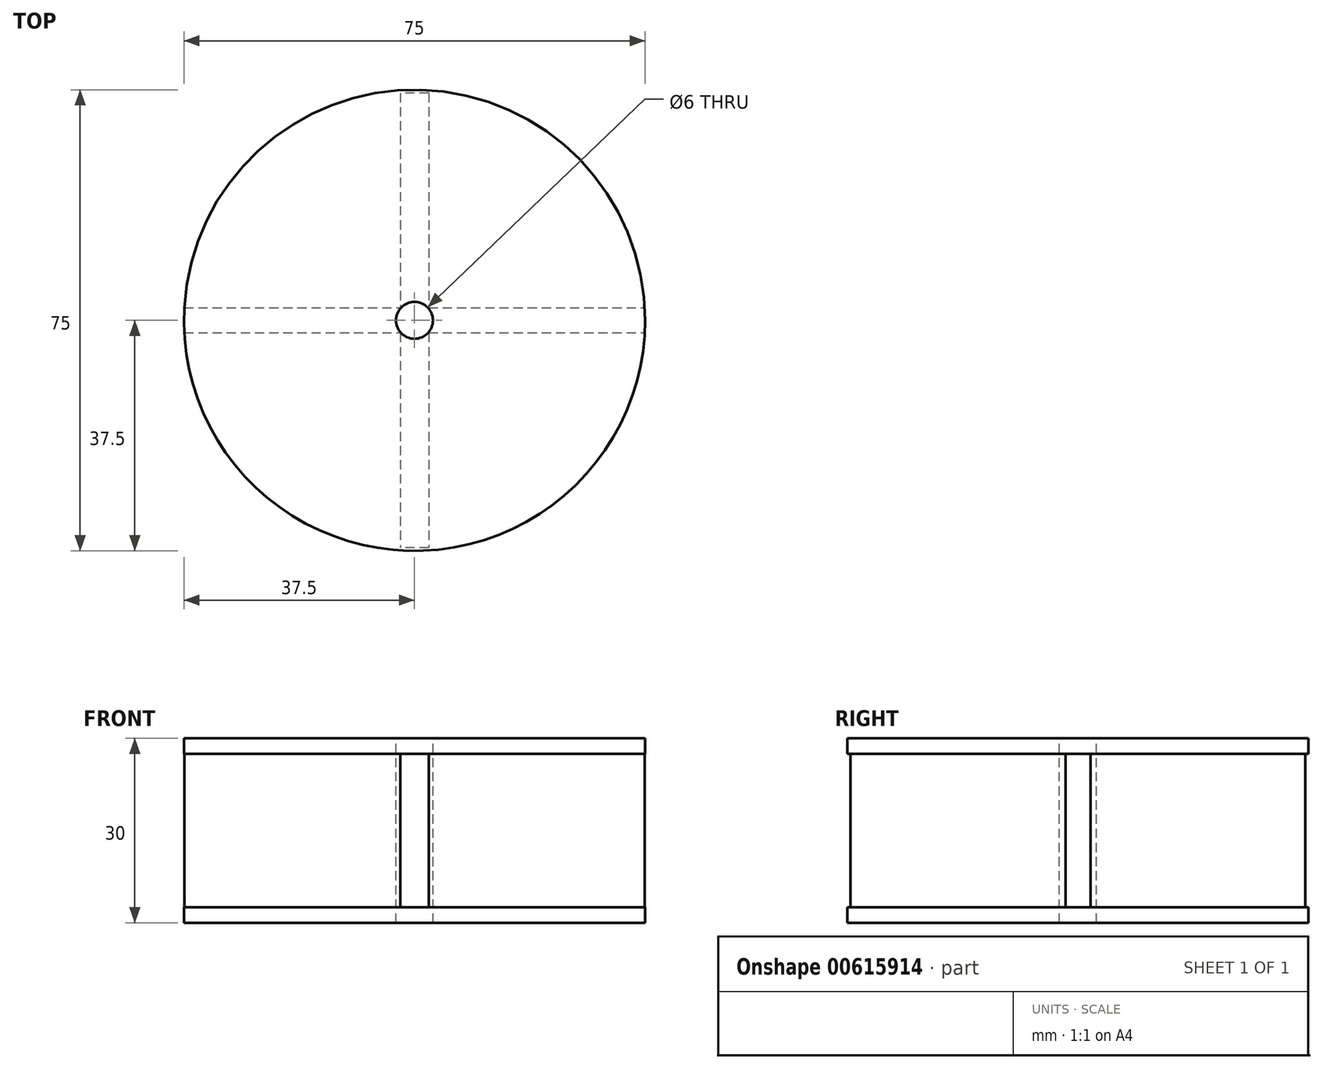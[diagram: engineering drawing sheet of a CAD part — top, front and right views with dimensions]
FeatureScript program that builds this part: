
annotation { "Feature Type Name" : "Feature", "Feature Type Description" : "" }
export const myFeature = defineFeature(function(context is Context, id is Id, definition is map)
    precondition{}
    {
        {
            var Q0;
            Q0=qCreatedBy(makeId("Top.planeOp"),FACE);
            var sketch = newSketch(context, id + "F0", { "sketchPlane" : qUnion([Q0])});
            skCircle(sketch, "E0", {"center": v(0, 0) * mm, "radius": 37.5 * mm});
            skSolve(sketch);
        }
        {
            var Q0;
            Q0 = qSketchRegion(id + "F0", true);
            extrude(context, id + "F1", {"entities" : qUnion([Q0]), "depth" : 2.5 * mm, "offsetDistance" : 25 * mm});
        }
        {
            var Q0;
            Q0=makeQuery(id+"F1.opExtrude","CAP_FACE",FACE,{"disambiguationData":[OSD([sQuery(id+"F0.wireOp",EDGE,"E0")])],"isStart":false});
            var sketch = newSketch(context, id + "F2", { "sketchPlane" : qUnion([Q0])});
            skLineSegment(sketch, "E1.bottom", {"start": v(-37.44, 2.03) * mm, "end": v(37.44, 2.03) * mm});
            skLineSegment(sketch, "E1.top", {"start": v(-37.44, -2.03) * mm, "end": v(37.44, -2.03) * mm});
            skLineSegment(sketch, "E1.left", {"start": v(-37.44, 2.03) * mm, "end": v(-37.44, -2.03) * mm});
            skLineSegment(sketch, "E1.right", {"start": v(37.44, 2.03) * mm, "end": v(37.44, -2.03) * mm});
            skPoint(sketch, "E1.middle", {"position": v(0, 0) * mm});
            skSolve(sketch);
        }
        {
            var Q0;
            Q0=makeQuery(id+"F2.imprint","IMPRINT",FACE,{"disambiguationData":[TD([[makeQuery(id+"F2.imprint","IMPRINT",EDGE,{"derivedFrom":sQuery(id+"F2.wireOp",EDGE,"E1.bottom")}),-1.0]])]});
            extrude(context, id + "F3", {"entities" : qUnion([Q0]), "operationType" : NewBodyOperationType.ADD, "depth" : 25 * mm, "offsetDistance" : 25 * mm});
        }
        {
            var Q0;
            {var subQ0=sQuery(id+"F0.wireOp",EDGE,"E0");var subQ1=makeQuery(id+"F1.opExtrude","CAP_FACE",FACE,{"disambiguationData":[OSD([subQ0])],"isStart":false});Q0=makeQuery(id+"F3.boolean.opBoolean","SPLIT",FACE,{"disambiguationData":[TD([makeQuery(id+"F1.opExtrude","SWEPT_FACE",FACE,{"disambiguationData":[OSD([subQ0])]}),subQ1,makeQuery(id+"F3.opExtrude","SWEPT_FACE",FACE,{"disambiguationData":[OSD([sQuery(id+"F2.wireOp",EDGE,"E1.top")])]}),makeQuery(id+"F3.opExtrude","SWEPT_FACE",FACE,{"disambiguationData":[OSD([sQuery(id+"F2.wireOp",EDGE,"E1.left")])]}),makeQuery(id+"F3.opExtrude","SWEPT_FACE",FACE,{"disambiguationData":[OSD([sQuery(id+"F2.wireOp",EDGE,"E1.right")])]})])],"derivedFrom":subQ1});}
            var sketch = newSketch(context, id + "F4", { "sketchPlane" : qUnion([Q0])});
            skLineSegment(sketch, "E2.bottom", {"start": v(2.3, 36.98) * mm, "end": v(-2.3, 36.98) * mm});
            skLineSegment(sketch, "E2.top", {"start": v(2.3, -36.98) * mm, "end": v(-2.3, -36.98) * mm});
            skLineSegment(sketch, "E2.left", {"start": v(2.3, 36.98) * mm, "end": v(2.3, -36.98) * mm});
            skLineSegment(sketch, "E2.right", {"start": v(-2.3, 36.98) * mm, "end": v(-2.3, -36.98) * mm});
            skPoint(sketch, "E2.middle", {"position": v(0, 0) * mm});
            skSolve(sketch);
        }
        {
            var Q0;
            Q0 = qSketchRegion(id + "F4", true);
            extrude(context, id + "F5", {"entities" : qUnion([Q0]), "operationType" : NewBodyOperationType.ADD, "depth" : 25 * mm, "offsetDistance" : 25 * mm});
        }
        {
            var Q0;
            Q0=makeQuery(id+"F5.boolean.opBoolean","MERGE",FACE,{"derivedFrom":[makeQuery(id+"F3.opExtrude","CAP_FACE",FACE,{"disambiguationData":[OSD([sQuery(id+"F2.wireOp",EDGE,"E1.bottom"),sQuery(id+"F2.wireOp",EDGE,"E1.top"),sQuery(id+"F2.wireOp",EDGE,"E1.left"),sQuery(id+"F2.wireOp",EDGE,"E1.right")])],"isStart":false}),makeQuery(id+"F5.opExtrude","CAP_FACE",FACE,{"disambiguationData":[OSD([sQuery(id+"F4.wireOp",EDGE,"E2.bottom"),sQuery(id+"F4.wireOp",EDGE,"E2.top"),sQuery(id+"F4.wireOp",EDGE,"E2.left"),sQuery(id+"F4.wireOp",EDGE,"E2.right")])],"isStart":false})]});
            var sketch = newSketch(context, id + "F6", { "sketchPlane" : qUnion([Q0])});
            skCircle(sketch, "E3", {"center": v(0, 0) * mm, "radius": 37.5 * mm});
            skSolve(sketch);
        }
        {
            var Q0;
            Q0 = qSketchRegion(id + "F6", true);
            extrude(context, id + "F7", {"entities" : qUnion([Q0]), "operationType" : NewBodyOperationType.ADD, "depth" : 2.5 * mm, "offsetDistance" : 25 * mm});
        }
        {
            var Q0;
            Q0=makeQuery(id+"F7.opExtrude","CAP_FACE",FACE,{"disambiguationData":[OSD([sQuery(id+"F6.wireOp",EDGE,"E3")])],"isStart":false});
            var sketch = newSketch(context, id + "F8", { "sketchPlane" : qUnion([Q0])});
            skPoint(sketch, "E4", {"position": v(0, 0) * mm});
            skSolve(sketch);
        }
        {
            var Q0;
            Q0=sQuery(id+"F8.wireOp",VERTEX,"E4");
            var Q1;
            Q1=makeQuery(id+"F1.opExtrude","SWEPT_BODY",BODY,{"disambiguationData":[OSD([sQuery(id+"F0.wireOp",EDGE,"E0")])]});
            hole(context, id + "F9", {"style" : HoleStyle.SIMPLE, "endStyle" : HoleEndStyle.THROUGH, "holeDiameter" : 6 * mm, "majorDiameter" : 5 * mm, "isTappedThrough" : true, "tappedDepth" : 12 * mm, "tapClearance" : 3, "locations" : qUnion([Q0]), "scope" : qUnion([Q1])});
        }
    });
